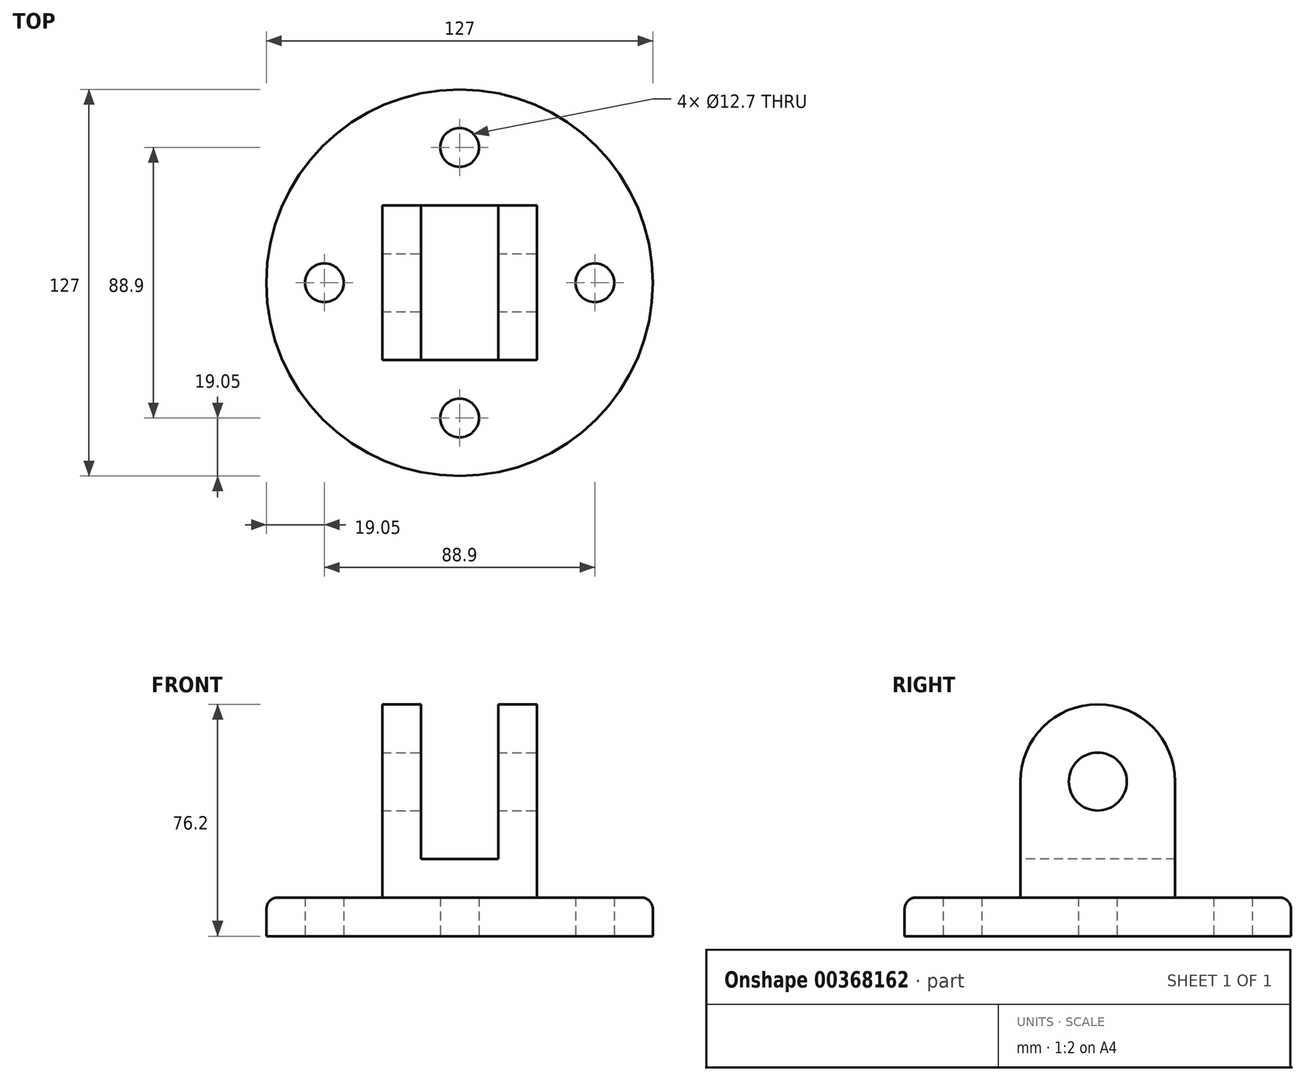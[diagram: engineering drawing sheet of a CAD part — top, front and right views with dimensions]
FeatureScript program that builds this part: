
annotation { "Feature Type Name" : "Feature", "Feature Type Description" : "" }
export const myFeature = defineFeature(function(context is Context, id is Id, definition is map)
    precondition{}
    {
        {
            var Q0;
            Q0=qCreatedBy(makeId("Top.planeOp"),FACE);
            var sketch = newSketch(context, id + "F0", { "sketchPlane" : qUnion([Q0])});
            skCircle(sketch, "E0", {"center": v(0, 0) * mm, "radius": 63.5 * mm});
            skCircle(sketch, "E1", {"center": v(0, 0) * mm, "radius": 44.45 * mm, "construction": true});
            skCircle(sketch, "E2", {"center": v(0, 44.45) * mm, "radius": 6.35 * mm});
            skCircle(sketch, "E3", {"center": v(-44.45, 0) * mm, "radius": 6.35 * mm});
            skCircle(sketch, "E4", {"center": v(44.45, 0) * mm, "radius": 6.35 * mm});
            skCircle(sketch, "E5", {"center": v(0, -44.45) * mm, "radius": 6.35 * mm});
            skSolve(sketch);
        }
        {
            var Q0;
            Q0 = qSketchRegion(id + "F0", true);
            extrude(context, id + "F1", {"entities" : qUnion([Q0]), "depth" : 12.7 * mm});
        }
        {
            var Q0;
            Q0=makeQuery(id+"F1.opExtrude","CAP_FACE",FACE,{"disambiguationData":[OSD([sQuery(id+"F0.wireOp",EDGE,"E0"),sQuery(id+"F0.wireOp",EDGE,"E2"),sQuery(id+"F0.wireOp",EDGE,"E3"),sQuery(id+"F0.wireOp",EDGE,"E4"),sQuery(id+"F0.wireOp",EDGE,"E5")])],"isStart":false});
            var sketch = newSketch(context, id + "F2", { "sketchPlane" : qUnion([Q0])});
            skLineSegment(sketch, "E6.bottom", {"start": v(-25.4, 25.4) * mm, "end": v(25.4, 25.4) * mm});
            skLineSegment(sketch, "E6.top", {"start": v(-25.4, -25.4) * mm, "end": v(25.4, -25.4) * mm});
            skLineSegment(sketch, "E6.left", {"start": v(-25.4, 25.4) * mm, "end": v(-25.4, -25.4) * mm});
            skLineSegment(sketch, "E6.right", {"start": v(25.4, 25.4) * mm, "end": v(25.4, -25.4) * mm});
            skSolve(sketch);
        }
        {
            var Q0;
            Q0 = qSketchRegion(id + "F2", true);
            extrude(context, id + "F3", {"entities" : qUnion([Q0]), "operationType" : NewBodyOperationType.ADD, "depth" : 12.7 * mm});
        }
        {
            var Q0;
            Q0=makeQuery(id+"F3.opExtrude","CAP_FACE",FACE,{"disambiguationData":[OSD([sQuery(id+"F2.wireOp",EDGE,"E6.bottom"),sQuery(id+"F2.wireOp",EDGE,"E6.top"),sQuery(id+"F2.wireOp",EDGE,"E6.left"),sQuery(id+"F2.wireOp",EDGE,"E6.right")])],"isStart":false});
            var sketch = newSketch(context, id + "F4", { "sketchPlane" : qUnion([Q0])});
            skLineSegment(sketch, "E7", {"start": v(-25.4, 25.4) * mm, "end": v(-12.7, 25.4) * mm});
            skLineSegment(sketch, "E8", {"start": v(-12.7, 25.4) * mm, "end": v(-12.7, -25.4) * mm});
            skLineSegment(sketch, "E9", {"start": v(-12.7, -25.4) * mm, "end": v(-25.4, -25.4) * mm});
            skLineSegment(sketch, "E10", {"start": v(-25.4, -25.4) * mm, "end": v(-25.4, 25.4) * mm});
            skLineSegment(sketch, "E11", {"start": v(25.4, 25.4) * mm, "end": v(12.7, 25.4) * mm});
            skLineSegment(sketch, "E12", {"start": v(12.7, 25.4) * mm, "end": v(12.7, -25.4) * mm});
            skLineSegment(sketch, "E13", {"start": v(12.7, -25.4) * mm, "end": v(25.4, -25.4) * mm});
            skLineSegment(sketch, "E14", {"start": v(25.4, -25.4) * mm, "end": v(25.4, 25.4) * mm});
            skSolve(sketch);
        }
        {
            var Q0;
            Q0 = qSketchRegion(id + "F4", true);
            extrude(context, id + "F5", {"entities" : qUnion([Q0]), "operationType" : NewBodyOperationType.ADD, "depth" : 25.4 * mm});
        }
        {
            var Q0;
            Q0=makeQuery(id+"F5.opExtrude","SWEPT_FACE",FACE,{"disambiguationData":[OSD([sQuery(id+"F4.wireOp",EDGE,"E12")])]});
            var sketch = newSketch(context, id + "F6", { "sketchPlane" : qUnion([Q0])});
            skArc(sketch, "E15", {"start": v(25.4, 50.8) * mm, "mid": v(0, 76.2) * mm, "end": v(-25.4, 50.8) * mm});
            skLineSegment(sketch, "E16", {"start": v(25.4, 50.8) * mm, "end": v(-25.4, 50.8) * mm});
            skSolve(sketch);
        }
        {
            var Q0;
            Q0 = qSketchRegion(id + "F6", true);
            extrude(context, id + "F7", {"entities" : qUnion([Q0]), "operationType" : NewBodyOperationType.ADD, "oppositeDirection" : true, "depth" : 12.7 * mm});
        }
        {
            var Q0;
            Q0=makeQuery(id+"F7.boolean.opBoolean","MERGE",FACE,{"derivedFrom":[makeQuery(id+"F5.boolean.opBoolean","MERGE",FACE,{"derivedFrom":[makeQuery(id+"F3.opExtrude","SWEPT_FACE",FACE,{"disambiguationData":[OSD([sQuery(id+"F2.wireOp",EDGE,"E6.right")])]}),makeQuery(id+"F5.opExtrude","SWEPT_FACE",FACE,{"disambiguationData":[OSD([sQuery(id+"F4.wireOp",EDGE,"E14")])]})]}),makeQuery(id+"F7.opExtrude","CAP_FACE",FACE,{"disambiguationData":[OSD([sQuery(id+"F6.wireOp",EDGE,"E15"),sQuery(id+"F6.wireOp",EDGE,"E16")])],"isStart":false})]});
            var sketch = newSketch(context, id + "F8", { "sketchPlane" : qUnion([Q0])});
            skCircle(sketch, "E17", {"center": v(0, 50.8) * mm, "radius": 9.53 * mm});
            skSolve(sketch);
        }
        {
            var Q0;
            Q0=makeQuery(id+"F5.boolean.opBoolean","MERGE",FACE,{"derivedFrom":[makeQuery(id+"F3.opExtrude","SWEPT_FACE",FACE,{"disambiguationData":[OSD([sQuery(id+"F2.wireOp",EDGE,"E6.left")])]}),makeQuery(id+"F5.opExtrude","SWEPT_FACE",FACE,{"disambiguationData":[OSD([sQuery(id+"F4.wireOp",EDGE,"E10")])]})]});
            var sketch = newSketch(context, id + "F9", { "sketchPlane" : qUnion([Q0])});
            skArc(sketch, "E18", {"start": v(25.4, 50.8) * mm, "mid": v(0, 76.2) * mm, "end": v(-25.4, 50.8) * mm});
            skLineSegment(sketch, "E19", {"start": v(-25.4, 50.8) * mm, "end": v(25.4, 50.8) * mm});
            skSolve(sketch);
        }
        {
            var Q0;
            Q0 = qSketchRegion(id + "F9", true);
            extrude(context, id + "F10", {"entities" : qUnion([Q0]), "operationType" : NewBodyOperationType.ADD, "oppositeDirection" : true, "depth" : 12.7 * mm});
        }
        {
            var Q0;
            Q0 = qSketchRegion(id + "F8", true);
            extrude(context, id + "F11", {"entities" : qUnion([Q0]), "operationType" : NewBodyOperationType.REMOVE, "endBound" : BoundingType.THROUGH_ALL, "oppositeDirection" : true, "depth" : 25.4 * mm});
        }
        {
            var Q0;
            Q0=makeQuery(id+"F1.opExtrude","CAP_EDGE",EDGE,{"disambiguationData":[OSD([sQuery(id+"F0.wireOp",EDGE,"E0")])],"isStart":false});
            var Q1;
            Q1=makeQuery(id+"F3.opExtrude","CAP_EDGE",EDGE,{"disambiguationData":[OSD([sQuery(id+"F2.wireOp",EDGE,"E6.left")])],"isStart":true});
            var Q2;
            Q2=makeQuery(id+"F3.opExtrude","CAP_EDGE",EDGE,{"disambiguationData":[OSD([sQuery(id+"F2.wireOp",EDGE,"E6.bottom")])],"isStart":true});
            var Q3;
            Q3=makeQuery(id+"F3.opExtrude","CAP_EDGE",EDGE,{"disambiguationData":[OSD([sQuery(id+"F2.wireOp",EDGE,"E6.right")])],"isStart":true});
            var Q4;
            Q4=makeQuery(id+"F3.opExtrude","CAP_EDGE",EDGE,{"disambiguationData":[OSD([sQuery(id+"F2.wireOp",EDGE,"E6.top")])],"isStart":true});
            fillet(context, id + "F12", {"entities" : qUnion([Q0, Q1, Q2, Q3, Q4]), "radius" : 3.8 * mm, "tangentPropagation" : true, "allowEdgeOverflow" : false});
        }
    });
